# Revit family: Legrand XL³-S 630 36 Modules à la rangée
name_source: partatom
category: Equipement électrique
units: mm (PartAtom-declared; Revit-internal decimal feet)

## family parameters
Basée sur le plan de construction = Non
Configuration du panneau = Deux colonnes, circuits au sein
Cote de connecteur circulaire = Utiliser le diamètre
Couper avec des vides une fois chargée = Non
Numéro OmniClass = 23.80.30.11.17
Partagée = Non
Point de calcul de pièce = Non
Titre OmniClass = Distribution Boards and Control Panels
Toujours verticalement = Oui
Type d'élément = Tableau de raccordement

## types (11) — shared parameters
Fabricant = Legrand
Hauteur Base = 100 mm  [stored 0.328084 ft]
IK = 08
IP = 40
Image du type = XL3S_630_36M_337583_p_230131.jpg
Largeur = 804 mm  [stored 2.6378 ft]
Largeur zone d'installation = 1302 mm  [stored 4.27165 ft]
Matière = Acier
RAL = 9003
URL = www.legrand.fr
distance avant zone d'installation = 804 mm  [stored 2.6378 ft]
distance coté zone d'installation = 249 mm  [stored 0.816929 ft]
kit finition = Non
kit finition 337960_337974 = Non
kit finition 337961_337974 = Non
kit finition 337962_337974 = Non
kit finition 337963_337974 = Non
kit finition 337964_337974 = Non
kit finition 337965_337974 = Non
kit finition 337966_337974 = Non
kit finition 337967_337974 = Non
kit finition 337968_337974 = Non
kit finition 337969_337974 = Non
kit finition 337970_337974 = Non
panneau latéral droit = Oui
panneau latéral gauche = Oui
porte = Oui
profondeur = 249 mm  [stored 0.816929 ft]
profondeur zone d'installation = 1053 mm
socle = Oui
zero-valued in all types: Elévation par défaut

## per-type parameters (varying)
- Enveloppe de distribution - XL³ S 630 - Coffret plastronnable - Métal - hauteur 750 - 36 modules: Conditions Générale d'Utilisation=https://export.legrand.com; Description=Ref 337523 - Enveloppe de distribution - XL³ S 630 - Coffret plastronnable - Métal - hauteur 750 - 36 modules; Hauteur=924 mm  [stored 3.0315 ft]; enveloppe 337523=Oui; enveloppe 337533=Non; enveloppe 337543=Non; enveloppe 337553=Non; enveloppe 337563=Non; enveloppe 337573=Non; enveloppe 337583=Non; enveloppe 337593=Non; enveloppe 337603=Non; enveloppe 337613=Non; enveloppe 337623=Non; panneau latéral droit 337862=Oui; panneau latéral droit 337863=Non; panneau latéral droit 337864=Non; panneau latéral droit 337865=Non; panneau latéral droit 337866=Non; panneau latéral droit 337867=Non; panneau latéral droit 337868=Non; panneau latéral droit 337869=Non; panneau latéral droit 337870=Non; panneau latéral droit 337871=Non; panneau latéral droit 337872=Non; panneau latéral gauche 337862=Oui; panneau latéral gauche 337863=Non; panneau latéral gauche 337864=Non; panneau latéral gauche 337865=Non; panneau latéral gauche 337866=Non; panneau latéral gauche 337867=Non; panneau latéral gauche 337868=Non; panneau latéral gauche 337869=Non; panneau latéral gauche 337870=Non; panneau latéral gauche 337871=Non; panneau latéral gauche 337872=Non; porte 337643=Oui; porte 337653=Non; porte 337663=Non; porte 337673=Non; porte 337683=Non; porte 337693=Non; porte 337703=Non; porte 337713=Non; porte 337723=Non; porte 337733=Non; porte 337743=Non
- Enveloppe de distribution - XL³ S 630 - Coffret plastronnable - Métal - hauteur 900 - 36 modules: Conditions Générale d'Utilisation=https://export.legrand.com; Description=Ref 337533 - Enveloppe de distribution - XL³ S 630 - Coffret plastronnable - Métal - hauteur 900 - 36 modules; Hauteur=1074 mm  [stored 3.52362 ft]; enveloppe 337523=Non; enveloppe 337533=Oui; enveloppe 337543=Non; enveloppe 337553=Non; enveloppe 337563=Non; enveloppe 337573=Non; enveloppe 337583=Non; enveloppe 337593=Non; enveloppe 337603=Non; enveloppe 337613=Non; enveloppe 337623=Non; panneau latéral droit 337862=Non; panneau latéral droit 337863=Oui; panneau latéral droit 337864=Non; panneau latéral droit 337865=Non; panneau latéral droit 337866=Non; panneau latéral droit 337867=Non; panneau latéral droit 337868=Non; panneau latéral droit 337869=Non; panneau latéral droit 337870=Non; panneau latéral droit 337871=Non; panneau latéral droit 337872=Non; panneau latéral gauche 337862=Non; panneau latéral gauche 337863=Oui; panneau latéral gauche 337864=Non; panneau latéral gauche 337865=Non; panneau latéral gauche 337866=Non; panneau latéral gauche 337867=Non; panneau latéral gauche 337868=Non; panneau latéral gauche 337869=Non; panneau latéral gauche 337870=Non; panneau latéral gauche 337871=Non; panneau latéral gauche 337872=Non; porte 337643=Non; porte 337653=Oui; porte 337663=Non; porte 337673=Non; porte 337683=Non; porte 337693=Non; porte 337703=Non; porte 337713=Non; porte 337723=Non; porte 337733=Non; porte 337743=Non
- Enveloppe de distribution - XL³ S 630 - Coffret plastronnable - Métal - hauteur 1050 - 36 modules: Conditions Générale d'Utilisation=https://export.legrand.com; Description=Ref 337543 - Enveloppe de distribution - XL³ S 630 - Coffret plastronnable - Métal - hauteur 1050 - 36 modules; Hauteur=1224 mm  [stored 4.01575 ft]; enveloppe 337523=Non; enveloppe 337533=Non; enveloppe 337543=Oui; enveloppe 337553=Non; enveloppe 337563=Non; enveloppe 337573=Non; enveloppe 337583=Non; enveloppe 337593=Non; enveloppe 337603=Non; enveloppe 337613=Non; enveloppe 337623=Non; panneau latéral droit 337862=Non; panneau latéral droit 337863=Non; panneau latéral droit 337864=Oui; panneau latéral droit 337865=Non; panneau latéral droit 337866=Non; panneau latéral droit 337867=Non; panneau latéral droit 337868=Non; panneau latéral droit 337869=Non; panneau latéral droit 337870=Non; panneau latéral droit 337871=Non; panneau latéral droit 337872=Non; panneau latéral gauche 337862=Non; panneau latéral gauche 337863=Non; panneau latéral gauche 337864=Oui; panneau latéral gauche 337865=Non; panneau latéral gauche 337866=Non; panneau latéral gauche 337867=Non; panneau latéral gauche 337868=Non; panneau latéral gauche 337869=Non; panneau latéral gauche 337870=Non; panneau latéral gauche 337871=Non; panneau latéral gauche 337872=Non; porte 337643=Non; porte 337653=Non; porte 337663=Oui; porte 337673=Non; porte 337683=Non; porte 337693=Non; porte 337703=Non; porte 337713=Non; porte 337723=Non; porte 337733=Non; porte 337743=Non
- Enveloppe de distribution - XL³ S 630 - Coffret plastronnable - Métal - hauteur 1200 - 36 modules: Conditions Générale d'Utilisation=https://export.legrand.com; Description=Ref 337553 - Enveloppe de distribution - XL³ S 630 - Coffret plastronnable - Métal - hauteur 1200 - 36 modules; Hauteur=1374 mm  [stored 4.50787 ft]; enveloppe 337523=Non; enveloppe 337533=Non; enveloppe 337543=Non; enveloppe 337553=Oui; enveloppe 337563=Non; enveloppe 337573=Non; enveloppe 337583=Non; enveloppe 337593=Non; enveloppe 337603=Non; enveloppe 337613=Non; enveloppe 337623=Non; panneau latéral droit 337862=Non; panneau latéral droit 337863=Non; panneau latéral droit 337864=Non; panneau latéral droit 337865=Oui; panneau latéral droit 337866=Non; panneau latéral droit 337867=Non; panneau latéral droit 337868=Non; panneau latéral droit 337869=Non; panneau latéral droit 337870=Non; panneau latéral droit 337871=Non; panneau latéral droit 337872=Non; panneau latéral gauche 337862=Non; panneau latéral gauche 337863=Non; panneau latéral gauche 337864=Non; panneau latéral gauche 337865=Oui; panneau latéral gauche 337866=Non; panneau latéral gauche 337867=Non; panneau latéral gauche 337868=Non; panneau latéral gauche 337869=Non; panneau latéral gauche 337870=Non; panneau latéral gauche 337871=Non; panneau latéral gauche 337872=Non; porte 337643=Non; porte 337653=Non; porte 337663=Non; porte 337673=Oui; porte 337683=Non; porte 337693=Non; porte 337703=Non; porte 337713=Non; porte 337723=Non; porte 337733=Non; porte 337743=Non
- Enveloppe de distribution - XL³ S 630 - Coffret plastronnable - Métal - hauteur 1350 - 36 modules: Conditions Générale d'Utilisation=https://export.legrand.com; Description=Ref 337563 -Enveloppe de distribution - XL³ S 630 - Coffret plastronnable - Métal - hauteur 1350 - 36 modules; Hauteur=1524 mm  [stored 5 ft]; enveloppe 337523=Non; enveloppe 337533=Non; enveloppe 337543=Non; enveloppe 337553=Non; enveloppe 337563=Oui; enveloppe 337573=Non; enveloppe 337583=Non; enveloppe 337593=Non; enveloppe 337603=Non; enveloppe 337613=Non; enveloppe 337623=Non; panneau latéral droit 337862=Non; panneau latéral droit 337863=Non; panneau latéral droit 337864=Non; panneau latéral droit 337865=Non; panneau latéral droit 337866=Oui; panneau latéral droit 337867=Non; panneau latéral droit 337868=Non; panneau latéral droit 337869=Non; panneau latéral droit 337870=Non; panneau latéral droit 337871=Non; panneau latéral droit 337872=Non; panneau latéral gauche 337862=Non; panneau latéral gauche 337863=Non; panneau latéral gauche 337864=Non; panneau latéral gauche 337865=Non; panneau latéral gauche 337866=Oui; panneau latéral gauche 337867=Non; panneau latéral gauche 337868=Non; panneau latéral gauche 337869=Non; panneau latéral gauche 337870=Non; panneau latéral gauche 337871=Non; panneau latéral gauche 337872=Non; porte 337643=Non; porte 337653=Non; porte 337663=Non; porte 337673=Non; porte 337683=Oui; porte 337693=Non; porte 337703=Non; porte 337713=Non; porte 337723=Non; porte 337733=Non; porte 337743=Non
- Enveloppe de distribution - XL³ S 630 - Coffret plastronnable - Métal - hauteur 1500 - 36 modules: Description=Ref 337573 -Enveloppe de distribution - XL³ S 630 - Coffret plastronnable - Métal - hauteur 1500 - 36 modules; Hauteur=1674 mm  [stored 5.49213 ft]; enveloppe 337523=Non; enveloppe 337533=Non; enveloppe 337543=Non; enveloppe 337553=Non; enveloppe 337563=Non; enveloppe 337573=Oui; enveloppe 337583=Non; enveloppe 337593=Non; enveloppe 337603=Non; enveloppe 337613=Non; enveloppe 337623=Non; panneau latéral droit 337862=Non; panneau latéral droit 337863=Non; panneau latéral droit 337864=Non; panneau latéral droit 337865=Non; panneau latéral droit 337866=Non; panneau latéral droit 337867=Oui; panneau latéral droit 337868=Non; panneau latéral droit 337869=Non; panneau latéral droit 337870=Non; panneau latéral droit 337871=Non; panneau latéral droit 337872=Non; panneau latéral gauche 337862=Non; panneau latéral gauche 337863=Non; panneau latéral gauche 337864=Non; panneau latéral gauche 337865=Non; panneau latéral gauche 337866=Non; panneau latéral gauche 337867=Oui; panneau latéral gauche 337868=Non; panneau latéral gauche 337869=Non; panneau latéral gauche 337870=Non; panneau latéral gauche 337871=Non; panneau latéral gauche 337872=Non; porte 337643=Non; porte 337653=Non; porte 337663=Non; porte 337673=Non; porte 337683=Non; porte 337693=Oui; porte 337703=Non; porte 337713=Non; porte 337723=Non; porte 337733=Non; porte 337743=Non
- Enveloppe de distribution - XL³ S 630 - Coffret plastronnable - Métal - hauteur 1650 - 36 modules: Conditions Générale d'Utilisation=https://export.legrand.com; Description=Ref 337583 - Enveloppe de distribution - XL³ S 630 - Coffret plastronnable - Métal - hauteur 1650 - 36 modules; Hauteur=1824 mm  [stored 5.98425 ft]; enveloppe 337523=Non; enveloppe 337533=Non; enveloppe 337543=Non; enveloppe 337553=Non; enveloppe 337563=Non; enveloppe 337573=Non; enveloppe 337583=Oui; enveloppe 337593=Non; enveloppe 337603=Non; enveloppe 337613=Non; enveloppe 337623=Non; panneau latéral droit 337862=Non; panneau latéral droit 337863=Non; panneau latéral droit 337864=Non; panneau latéral droit 337865=Non; panneau latéral droit 337866=Non; panneau latéral droit 337867=Non; panneau latéral droit 337868=Oui; panneau latéral droit 337869=Non; panneau latéral droit 337870=Non; panneau latéral droit 337871=Non; panneau latéral droit 337872=Non; panneau latéral gauche 337862=Non; panneau latéral gauche 337863=Non; panneau latéral gauche 337864=Non; panneau latéral gauche 337865=Non; panneau latéral gauche 337866=Non; panneau latéral gauche 337867=Non; panneau latéral gauche 337868=Oui; panneau latéral gauche 337869=Non; panneau latéral gauche 337870=Non; panneau latéral gauche 337871=Non; panneau latéral gauche 337872=Non; porte 337643=Non; porte 337653=Non; porte 337663=Non; porte 337673=Non; porte 337683=Non; porte 337693=Non; porte 337703=Oui; porte 337713=Non; porte 337723=Non; porte 337733=Non; porte 337743=Non
- Enveloppe de distribution - XL³ S 630 - Coffret plastronnable - Métal - hauteur 1800 - 36 modules: Conditions Générale d'Utilisation=https://export.legrand.com; Description=Ref 337593 - Enveloppe de distribution - XL³ S 630 - Coffret plastronnable - Métal - hauteur 1800 - 36 modules; Hauteur=1974 mm  [stored 6.47638 ft]; enveloppe 337523=Non; enveloppe 337533=Non; enveloppe 337543=Non; enveloppe 337553=Non; enveloppe 337563=Non; enveloppe 337573=Non; enveloppe 337583=Non; enveloppe 337593=Oui; enveloppe 337603=Non; enveloppe 337613=Non; enveloppe 337623=Non; panneau latéral droit 337862=Non; panneau latéral droit 337863=Non; panneau latéral droit 337864=Non; panneau latéral droit 337865=Non; panneau latéral droit 337866=Non; panneau latéral droit 337867=Non; panneau latéral droit 337868=Non; panneau latéral droit 337869=Oui; panneau latéral droit 337870=Non; panneau latéral droit 337871=Non; panneau latéral droit 337872=Non; panneau latéral gauche 337862=Non; panneau latéral gauche 337863=Non; panneau latéral gauche 337864=Non; panneau latéral gauche 337865=Non; panneau latéral gauche 337866=Non; panneau latéral gauche 337867=Non; panneau latéral gauche 337868=Non; panneau latéral gauche 337869=Oui; panneau latéral gauche 337870=Non; panneau latéral gauche 337871=Non; panneau latéral gauche 337872=Non; porte 337643=Non; porte 337653=Non; porte 337663=Non; porte 337673=Non; porte 337683=Non; porte 337693=Non; porte 337703=Non; porte 337713=Oui; porte 337723=Non; porte 337733=Non; porte 337743=Non
- Enveloppe de distribution - XL³ S 630 - Coffret plastronnable - Métal - hauteur 1950 - 36 modules: Conditions Générale d'Utilisation=https://export.legrand.com; Description=Ref 337603 - Enveloppe de distribution - XL³ S 630 - Coffret plastronnable - Métal - hauteur 1950 - 36 modules; Hauteur=2124 mm  [stored 6.9685 ft]; enveloppe 337523=Non; enveloppe 337533=Non; enveloppe 337543=Non; enveloppe 337553=Non; enveloppe 337563=Non; enveloppe 337573=Non; enveloppe 337583=Non; enveloppe 337593=Non; enveloppe 337603=Oui; enveloppe 337613=Non; enveloppe 337623=Non; panneau latéral droit 337862=Non; panneau latéral droit 337863=Non; panneau latéral droit 337864=Non; panneau latéral droit 337865=Non; panneau latéral droit 337866=Non; panneau latéral droit 337867=Non; panneau latéral droit 337868=Non; panneau latéral droit 337869=Non; panneau latéral droit 337870=Oui; panneau latéral droit 337871=Non; panneau latéral droit 337872=Non; panneau latéral gauche 337862=Non; panneau latéral gauche 337863=Non; panneau latéral gauche 337864=Non; panneau latéral gauche 337865=Non; panneau latéral gauche 337866=Non; panneau latéral gauche 337867=Non; panneau latéral gauche 337868=Non; panneau latéral gauche 337869=Non; panneau latéral gauche 337870=Oui; panneau latéral gauche 337871=Non; panneau latéral gauche 337872=Non; porte 337643=Non; porte 337653=Non; porte 337663=Non; porte 337673=Non; porte 337683=Non; porte 337693=Non; porte 337703=Non; porte 337713=Non; porte 337723=Oui; porte 337733=Non; porte 337743=Non
- Enveloppe de distribution - XL³ S 630 - Coffret plastronnable - Métal - hauteur 2100 - 36 modules: Conditions Générale d'Utilisation=https://export.legrand.com; Description=Ref 337613 - Enveloppe de distribution - XL³ S 630 - Coffret plastronnable - Métal - hauteur 2100 - 36 modules; Hauteur=2274 mm  [stored 7.46063 ft]; enveloppe 337523=Non; enveloppe 337533=Non; enveloppe 337543=Non; enveloppe 337553=Non; enveloppe 337563=Non; enveloppe 337573=Non; enveloppe 337583=Non; enveloppe 337593=Non; enveloppe 337603=Non; enveloppe 337613=Oui; enveloppe 337623=Non; panneau latéral droit 337862=Non; panneau latéral droit 337863=Non; panneau latéral droit 337864=Non; panneau latéral droit 337865=Non; panneau latéral droit 337866=Non; panneau latéral droit 337867=Non; panneau latéral droit 337868=Non; panneau latéral droit 337869=Non; panneau latéral droit 337870=Non; panneau latéral droit 337871=Oui; panneau latéral droit 337872=Non; panneau latéral gauche 337862=Non; panneau latéral gauche 337863=Non; panneau latéral gauche 337864=Non; panneau latéral gauche 337865=Non; panneau latéral gauche 337866=Non; panneau latéral gauche 337867=Non; panneau latéral gauche 337868=Non; panneau latéral gauche 337869=Non; panneau latéral gauche 337870=Non; panneau latéral gauche 337871=Oui; panneau latéral gauche 337872=Non; porte 337643=Non; porte 337653=Non; porte 337663=Non; porte 337673=Non; porte 337683=Non; porte 337693=Non; porte 337703=Non; porte 337713=Non; porte 337723=Non; porte 337733=Oui; porte 337743=Non
- Enveloppe de distribution - XL³ S 630 - Coffret plastronnable - Métal - hauteur 2250 - 36 modules: Conditions Générale d'Utilisation=https://export.legrand.com; Description=Ref 337623 - Enveloppe de distribution - XL³ S 630 - Coffret plastronnable - Métal - hauteur 2250 - 36 modules; Hauteur=2424 mm  [stored 7.95276 ft]; enveloppe 337523=Non; enveloppe 337533=Non; enveloppe 337543=Non; enveloppe 337553=Non; enveloppe 337563=Non; enveloppe 337573=Non; enveloppe 337583=Non; enveloppe 337593=Non; enveloppe 337603=Non; enveloppe 337613=Non; enveloppe 337623=Oui; panneau latéral droit 337862=Non; panneau latéral droit 337863=Non; panneau latéral droit 337864=Non; panneau latéral droit 337865=Non; panneau latéral droit 337866=Non; panneau latéral droit 337867=Non; panneau latéral droit 337868=Non; panneau latéral droit 337869=Non; panneau latéral droit 337870=Non; panneau latéral droit 337871=Non; panneau latéral droit 337872=Oui; panneau latéral gauche 337862=Non; panneau latéral gauche 337863=Non; panneau latéral gauche 337864=Non; panneau latéral gauche 337865=Non; panneau latéral gauche 337866=Non; panneau latéral gauche 337867=Non; panneau latéral gauche 337868=Non; panneau latéral gauche 337869=Non; panneau latéral gauche 337870=Non; panneau latéral gauche 337871=Non; panneau latéral gauche 337872=Oui; porte 337643=Non; porte 337653=Non; porte 337663=Non; porte 337673=Non; porte 337683=Non; porte 337693=Non; porte 337703=Non; porte 337713=Non; porte 337723=Non; porte 337733=Non; porte 337743=Oui

note: [stored X ft] marks values corroborated as IEEE doubles in the binary element streams (Revit-internal decimal feet)
